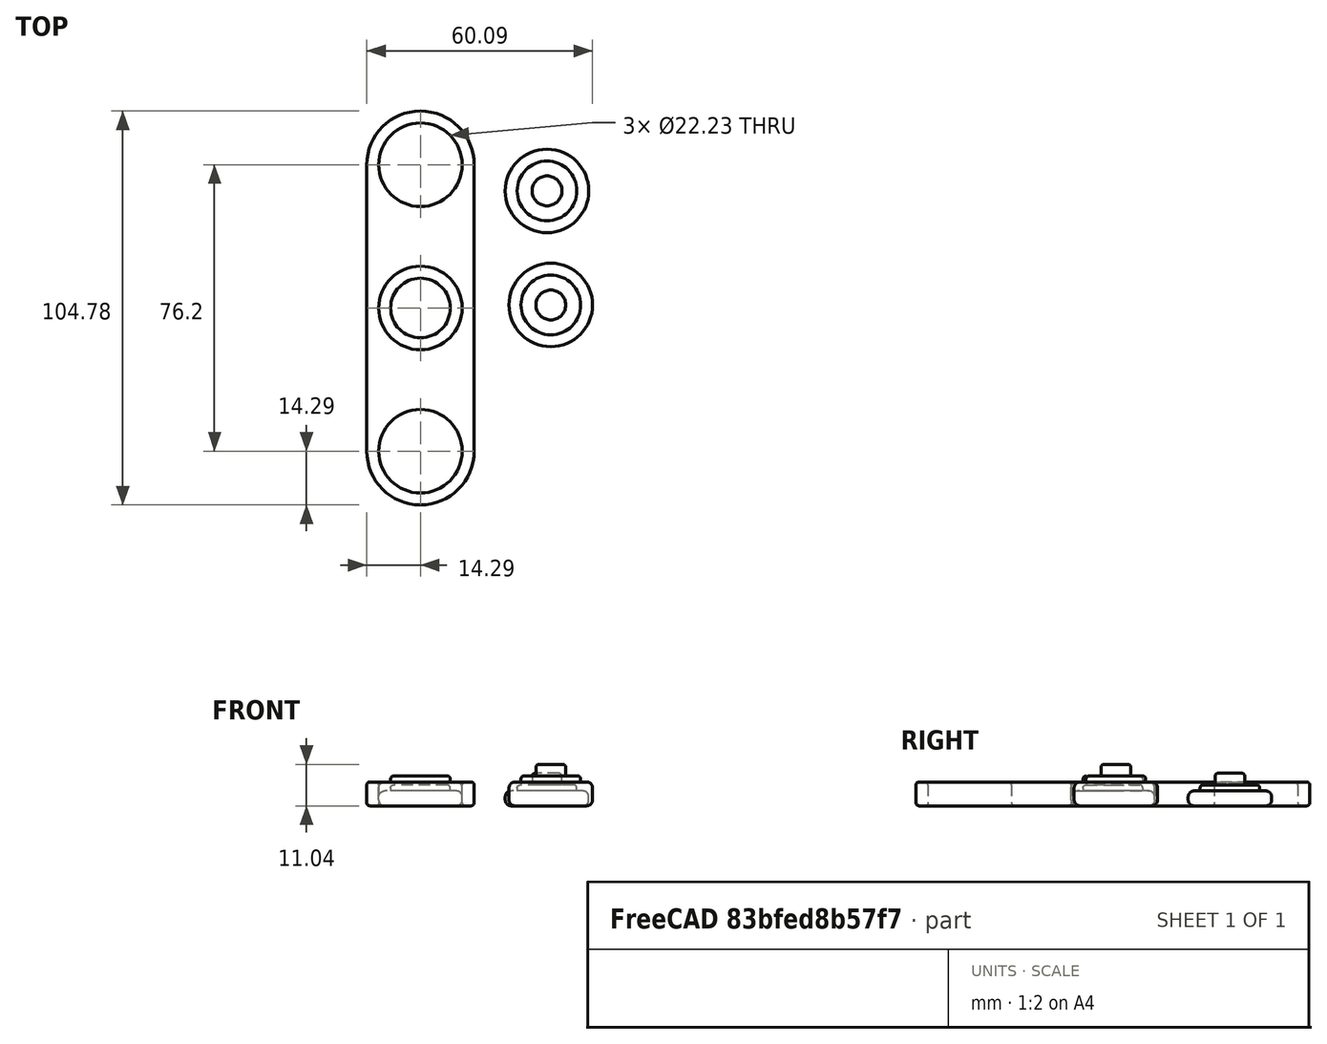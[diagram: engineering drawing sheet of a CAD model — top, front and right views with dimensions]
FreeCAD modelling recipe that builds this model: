
FCSTD DOCUMENT  (FreeCAD 0.16R6706 (Git))
Label: two-arm-spinner
License: All rights reserved
LicenseURL: http://en.wikipedia.org/wiki/All_rights_reserved
objects: PartDesign::Fillet×10, Sketcher::SketchObject×5, PartDesign::Pad×5, Part::Cylinder×2
note: 27 computed .brp shape members not serialized (recipe doc carries the construction recipe); baked Part::Feature solids carry a one-line shape summary decoded from their .brp

FEATURE [Part::Cylinder] Cylinder
  Angle = 360
  Height = 3.96875
  Radius = 11.1125
FEATURE [PartDesign::Fillet] Fillet
  Base = -> Cylinder [Edge1]
  Radius = 1.5875
FEATURE [PartDesign::Fillet] Fillet001
  Base = -> Fillet [Edge3]
  Radius = 1.5875
FEATURE [Sketcher::SketchObject] Sketch
  Placement = pos=(0,0,3.96875) rot=(0,0,1;0rad)
  Support = -> Fillet001 [Face5]
  sketch-geometry (1):
    g0: Circle CenterX=0 CenterY=0 CenterZ=0 NormalX=0 NormalY=0 NormalZ=1 Radius=7.9375
  constraints (2):
    c: Coincident(g0,g-1)
    c: Radius(g0) = 7.9375
FEATURE [PartDesign::Pad] Pad
  Length = 1.5875
  Length2 = 3.175
  Sketch = -> Sketch
  Type = 0
FEATURE [PartDesign::Fillet] Fillet002
  Base = -> Pad [Edge1]
  Radius = 0.79375
FEATURE [Sketcher::SketchObject] Sketch001
  Placement = pos=(0,0,5.55625) rot=(0,0,1;0rad)
  Support = -> Fillet002 [Face1]
  sketch-geometry (1):
    g0: Circle CenterX=0 CenterY=0 CenterZ=0 NormalX=0 NormalY=0 NormalZ=1 Radius=3.96875
  constraints (2):
    c: Coincident(g0,g-1)
    c: Radius(g0) = 3.96875
FEATURE [PartDesign::Pad] Pad001
  Length = 3.1
  Length2 = 100
  Sketch = -> Sketch001
  Type = 0
FEATURE [PartDesign::Fillet] Fillet003  label="Plug"
  Base = -> Pad001 [Edge1]
  Placement = pos=(33.6761,31.1408,-0.00103356) rot=(0,0,1;0rad)
  Radius = 0.79375
FEATURE [Sketcher::SketchObject] Sketch002
  sketch-geometry (7):
    g0: ArcOfCircle CenterX=0 CenterY=38.1 CenterZ=0 NormalX=0 NormalY=0 NormalZ=1 Radius=14.2875 StartAngle=0 EndAngle=3.14159
    g1: ArcOfCircle CenterX=0 CenterY=-38.1 CenterZ=0 NormalX=0 NormalY=0 NormalZ=1 Radius=14.2875 StartAngle=3.14159 EndAngle=6.28319
    g2: LineSegment StartX=-14.2875 StartY=38.1 StartZ=0 EndX=-14.2875 EndY=-38.1 EndZ=0
    g3: LineSegment StartX=14.2875 StartY=38.1 StartZ=0 EndX=14.2875 EndY=-38.1 EndZ=0
    g4: Circle CenterX=0 CenterY=38.1 CenterZ=0 NormalX=0 NormalY=0 NormalZ=1 Radius=11.1125
    g5: Circle CenterX=0 CenterY=-38.1 CenterZ=0 NormalX=0 NormalY=0 NormalZ=1 Radius=11.1125
    g6: Circle CenterX=0 CenterY=0 CenterZ=0 NormalX=0 NormalY=0 NormalZ=1 Radius=11.1125
  constraints (17):
    c: Tangent(g0,g3) = 1.5708
    c: Tangent(g0,g2) = -1.5708
    c: Tangent(g2,g1) = -1.5708
    c: Tangent(g3,g1) = 1.5708
    c: Vertical(g2)
    c: Equal(g0,g1)
    c: PointOnObject(g0,g-2)
    c: Coincident(g5,g1)
    c: PointOnObject(g6,g-1)
    c: DistanceX(g0,g6) = 0
    c: DistanceY(g-1,g0) = 38.1
    c: DistanceY(g1,g-1) = 38.1
    c: Radius(g5) = 11.1125
    c: Radius(g6) = 11.1125
    c: Radius(g4) = 11.1125
    c: DistanceX(g1,g1) = 14.2875
    c: Coincident(g0,g4)
FEATURE [PartDesign::Pad] Pad002
  Length = 6.35
  Length2 = 100
  Sketch = -> Sketch002
  Type = 0
FEATURE [PartDesign::Fillet] Fillet004
  Base = -> Pad002 [Edge3,Edge6,Edge9,Edge11,Edge14,Edge17,Edge20]
  Radius = 0.79375
FEATURE [PartDesign::Fillet] Fillet005  label="Spinner"
  Base = -> Fillet004 [Edge3,Edge11,Edge12,Edge6,Edge13,Edge14,Edge15]
  Radius = 0.79375
FEATURE [Part::Cylinder] Cylinder001
  Angle = 360
  Height = 6.35
  Radius = 11.1125
FEATURE [PartDesign::Fillet] Fillet006
  Base = -> Cylinder001 [Edge1]
  Radius = 1.5875
FEATURE [PartDesign::Fillet] Fillet007
  Base = -> Fillet006 [Edge3]
  Radius = 1.5875
FEATURE [Sketcher::SketchObject] Sketch003
  Placement = pos=(0,0,6.35) rot=(0,0,1;0rad)
  Support = -> Fillet007 [Face5]
  sketch-geometry (1):
    g0: Circle CenterX=0 CenterY=0 CenterZ=0 NormalX=0 NormalY=0 NormalZ=1 Radius=7.9375
  constraints (2):
    c: Coincident(g0,g-1)
    c: Radius(g0) = 7.9375
FEATURE [PartDesign::Pad] Pad003
  Length = 1.5875
  Length2 = 3.175
  Sketch = -> Sketch003
  Type = 0
FEATURE [PartDesign::Fillet] Fillet008
  Base = -> Pad003 [Edge1]
  Radius = 0.79375
FEATURE [Sketcher::SketchObject] Sketch004
  Placement = pos=(0,0,7.9375) rot=(0,0,1;0rad)
  Support = -> Fillet008 [Face1]
  sketch-geometry (1):
    g0: Circle CenterX=0 CenterY=0 CenterZ=0 NormalX=0 NormalY=0 NormalZ=1 Radius=3.96875
  constraints (2):
    c: Coincident(g0,g-1)
    c: Radius(g0) = 3.96875
FEATURE [PartDesign::Pad] Pad004
  Length = 3.1
  Length2 = 100
  Sketch = -> Sketch004
  Type = 0
FEATURE [PartDesign::Fillet] Fillet009  label="Stand"
  Base = -> Pad004 [Edge1]
  Placement = pos=(34.6846,0.799578,1.38991e-05) rot=(0,0,1;0rad)
  Radius = 0.79375
